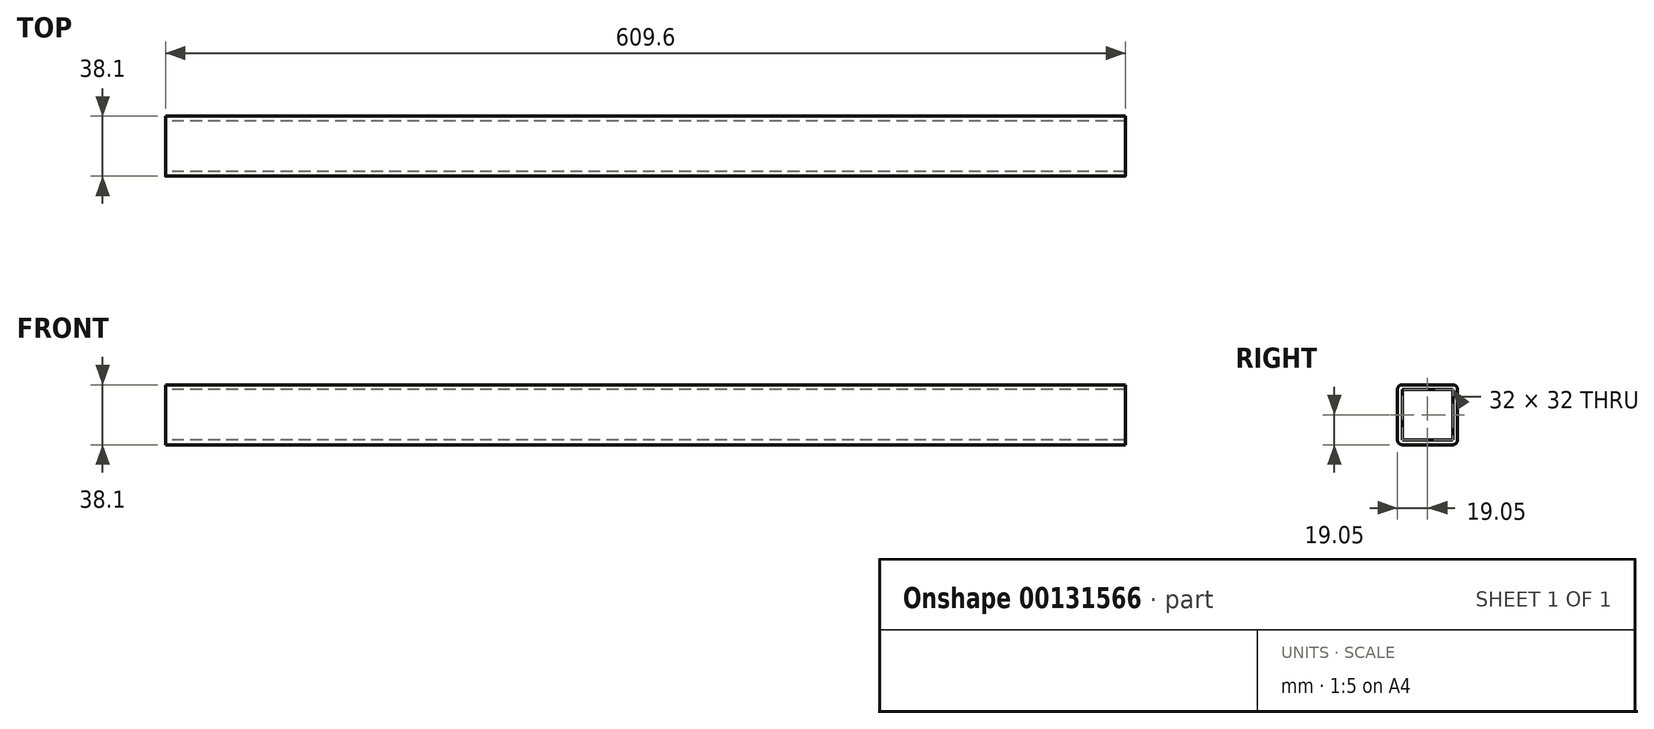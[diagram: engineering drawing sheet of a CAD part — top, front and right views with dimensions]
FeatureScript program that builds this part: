
annotation { "Feature Type Name" : "Feature", "Feature Type Description" : "" }
export const myFeature = defineFeature(function(context is Context, id is Id, definition is map)
    precondition{}
    {
        {
            var Q0;
            Q0=qCreatedBy(makeId("Right.planeOp"),FACE);
            var sketch = newSketch(context, id + "F0", { "sketchPlane" : qUnion([Q0])});
            skLineSegment(sketch, "E0.bottom", {"start": v(16, 19.05) * mm, "end": v(-16, 19.05) * mm});
            skLineSegment(sketch, "E0.top", {"start": v(16, -19.05) * mm, "end": v(-16, -19.05) * mm});
            skLineSegment(sketch, "E0.left", {"start": v(19.05, 16) * mm, "end": v(19.05, -16) * mm});
            skLineSegment(sketch, "E0.right", {"start": v(-19.05, 16) * mm, "end": v(-19.05, -16) * mm});
            skPoint(sketch, "E0.middle", {"position": v(0, 0) * mm});
            skPoint(sketch, "E1.visualSharp", {"position": v(-19.05, 19.05) * mm});
            skArc(sketch, "E1.filletArc", {"start": v(-16, 19.05) * mm, "mid": v(-18.16, 18.16) * mm, "end": v(-19.05, 16) * mm});
            skPoint(sketch, "E2.visualSharp", {"position": v(19.05, 19.05) * mm});
            skArc(sketch, "E2.filletArc", {"start": v(19.05, 16) * mm, "mid": v(18.16, 18.16) * mm, "end": v(16, 19.05) * mm});
            skPoint(sketch, "E3.visualSharp", {"position": v(19.05, -19.05) * mm});
            skArc(sketch, "E3.filletArc", {"start": v(16, -19.05) * mm, "mid": v(18.16, -18.16) * mm, "end": v(19.05, -16) * mm});
            skPoint(sketch, "E4.visualSharp", {"position": v(-19.05, -19.05) * mm});
            skArc(sketch, "E4.filletArc", {"start": v(-19.05, -16) * mm, "mid": v(-18.16, -18.16) * mm, "end": v(-16, -19.05) * mm});
            skLineSegment(sketch, "E5.bottom", {"start": v(16, 16) * mm, "end": v(-16, 16) * mm});
            skLineSegment(sketch, "E5.top", {"start": v(16, -16) * mm, "end": v(-16, -16) * mm});
            skLineSegment(sketch, "E5.left", {"start": v(16, 16) * mm, "end": v(16, -16) * mm});
            skLineSegment(sketch, "E5.right", {"start": v(-16, 16) * mm, "end": v(-16, -16) * mm});
            skSolve(sketch);
        }
        {
            var Q0;
            Q0=makeQuery(id+"F0.imprint","IMPRINT",FACE,{"disambiguationData":[TD([[makeQuery(id+"F0.imprint","IMPRINT",EDGE,{"derivedFrom":sQuery(id+"F0.wireOp",EDGE,"E0.bottom")}),1.0]])]});
            extrude(context, id + "F1", {"entities" : qUnion([Q0]), "depth" : 609.6 * mm});
        }
    });
